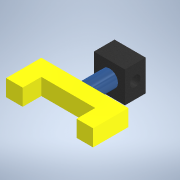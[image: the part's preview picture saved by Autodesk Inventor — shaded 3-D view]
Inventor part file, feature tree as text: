
AUTODESK INVENTOR PART (.ipt)
format: ipt  version: 2021 (Build 250183000, 183)  size: 147,968 bytes
history: native  units: mm
features: extrude x5, sketch x5
ambient origin geometry x8: Origin, YZ Plane, XZ Plane, XY Plane, X Axis, Y Axis, Z Axis, Center Point
bodies: Solid1 (feature_tree)
feature tree (10):
  extrude  "Extrusion1"  Depth=150.0mm
  extrude  "Extrusion2"  Depth=80.0mm
  extrude  "Extrusion3"  Depth=420.0mm
  extrude  "Extrusion4"  Depth=80.0mm TaperAngle=0.0deg
  extrude  "Extrusion5"  Depth=80.0mm
  sketch  "Sketch1"  dims[d0=150.0mm d1=150.0mm]
  sketch  "Sketch2"  dims[d2=100.0mm d3=0.0mm d4=80.0mm]
  sketch  "Sketch3"  dims[d5=120.0mm d6=0.0mm d7=420.0mm]
  sketch  "Sketch4"  dims[d8=80.0mm d9=80.0mm d10=0.0mm]
  sketch  "Sketch5"  dims[d11=80.0mm d12=80.0mm d13=90.0mm d14=0.0mm d15=50.0mm d16=500.0mm d17=0.0mm]
